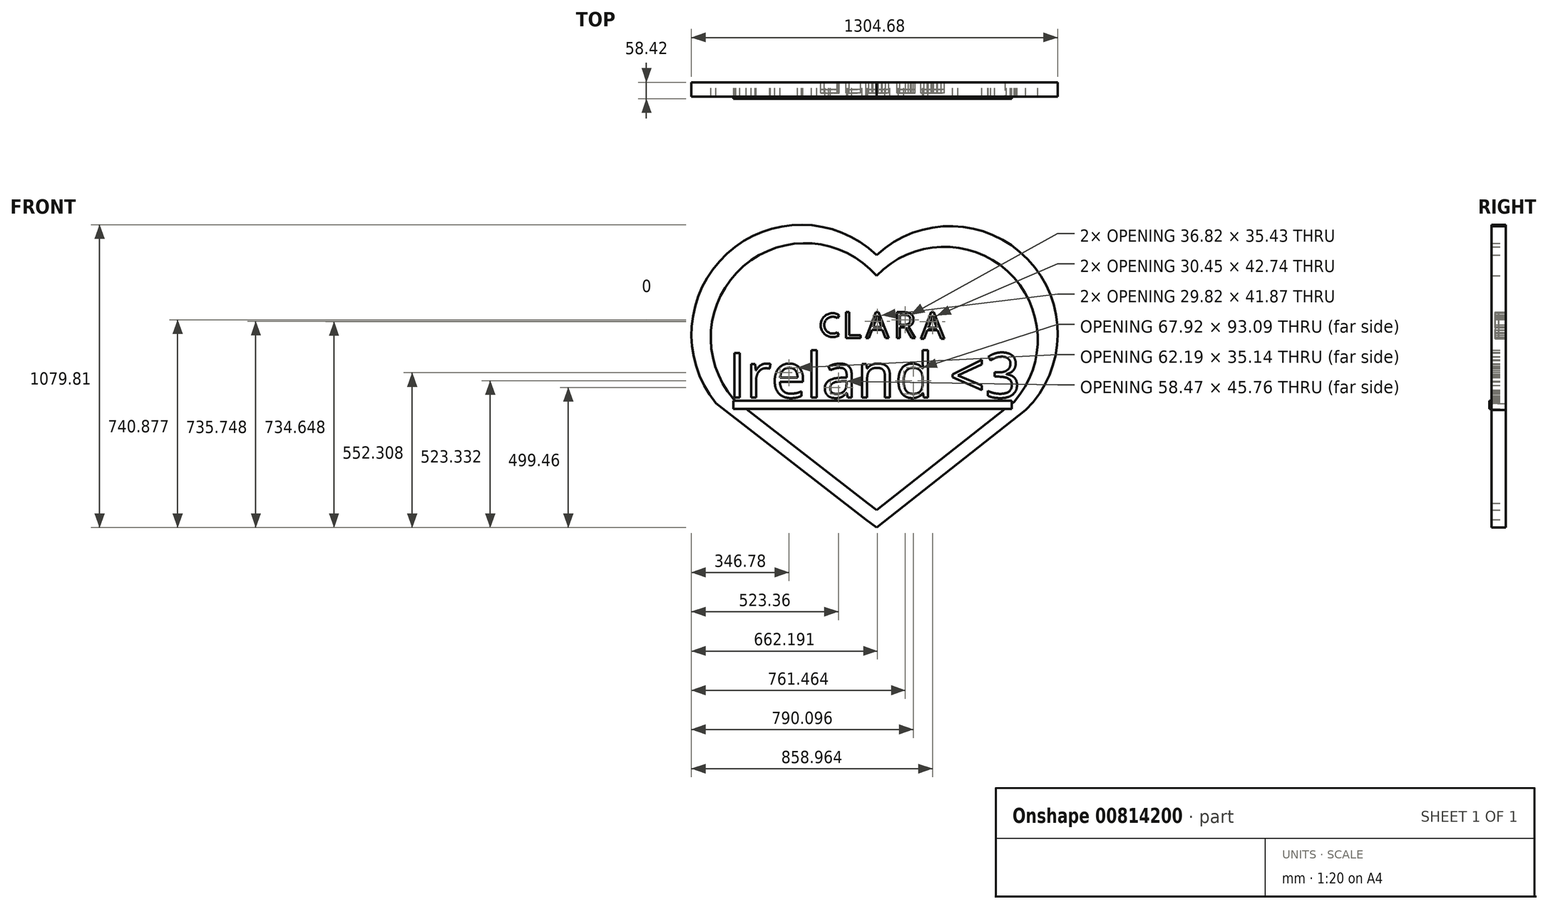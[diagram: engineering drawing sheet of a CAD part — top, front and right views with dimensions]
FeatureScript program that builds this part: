
annotation { "Feature Type Name" : "Feature", "Feature Type Description" : "" }
export const myFeature = defineFeature(function(context is Context, id is Id, definition is map)
    precondition{}
    {
        {
            var Q0;
            Q0=qCreatedBy(makeId("Front.planeOp"),FACE);
            var sketch = newSketch(context, id + "F0", { "sketchPlane" : qUnion([Q0])});
            skArc(sketch, "E0", {"start": v(-133.41, 53.67) * mm, "mid": v(-199.68, 18.4) * mm, "end": v(-134.37, -18.62) * mm});
            skArc(sketch, "E1", {"start": v(-140.44, 43.1) * mm, "mid": v(-186.97, 18.55) * mm, "end": v(-141.67, -8.19) * mm});
            skLineSegment(sketch, "E2", {"start": v(-140.44, 43.1) * mm, "end": v(-133.41, 53.67) * mm});
            skLineSegment(sketch, "E3", {"start": v(-141.67, -8.19) * mm, "end": v(-134.37, -18.62) * mm});
            skText(sketch, "E4", { "text": "R\n", "fontName": "OpenSans-Regular.ttf"});
            skText(sketch, "E5", { "text": "A", "fontName": "OpenSans-Regular.ttf"});
            skText(sketch, "E6", { "text": "A", "fontName": "OpenSans-Regular.ttf"});
            skText(sketch, "E7", { "text": "L", "fontName": "OpenSans-Regular.ttf"});
            const initialGuessF0  = {"E4": [0.05946, -0.02868, 1, 0, 0.09344], "E5": [0.15712, -0.03057, 1, 0, 0.09492], "E6": [-0.0388, -0.02822, 1, 0, 0.09298], "E7": [-0.12193, -0.02824, 1, 0, 0.093]};
            skSetInitialGuess(sketch, initialGuessF0);
            skSolve(sketch);
        }
        {
            var Q0;
            Q0 = qSketchRegion(id + "F0", true);
            extrude(context, id + "F1", {"entities" : qUnion([Q0]), "depth" : 25.4 * mm, "offsetDistance" : 25.4 * mm});
        }
        {
            var Q0;
            Q0=makeQuery(id+"F1.opExtrude","CAP_FACE",FACE,{"disambiguationData":[OSD([sQuery(id+"F0.wireOp",EDGE,"E0"),sQuery(id+"F0.wireOp",EDGE,"E1"),sQuery(id+"F0.wireOp",EDGE,"E2"),sQuery(id+"F0.wireOp",EDGE,"E3")])],"isStart":false});
            var Q1;
            Q1=makeQuery(id+"F1.opExtrude","CAP_FACE",FACE,{"disambiguationData":[OSD([sQuery(id+"F0.wireOp",EDGE,"E7.sketch_text.stroke-0"),sQuery(id+"F0.wireOp",EDGE,"E7.sketch_text.stroke-1"),sQuery(id+"F0.wireOp",EDGE,"E7.sketch_text.stroke-2"),sQuery(id+"F0.wireOp",EDGE,"E7.sketch_text.stroke-3"),sQuery(id+"F0.wireOp",EDGE,"E7.sketch_text.stroke-4"),sQuery(id+"F0.wireOp",EDGE,"E7.sketch_text.stroke-5")])],"isStart":false});
            var Q2;
            Q2=makeQuery(id+"F1.opExtrude","CAP_FACE",FACE,{"disambiguationData":[OSD([sQuery(id+"F0.wireOp",EDGE,"E6.sketch_text.stroke-0"),sQuery(id+"F0.wireOp",EDGE,"E6.sketch_text.stroke-1"),sQuery(id+"F0.wireOp",EDGE,"E6.sketch_text.stroke-2"),sQuery(id+"F0.wireOp",EDGE,"E6.sketch_text.stroke-3"),sQuery(id+"F0.wireOp",EDGE,"E6.sketch_text.stroke-4"),sQuery(id+"F0.wireOp",EDGE,"E6.sketch_text.stroke-5"),sQuery(id+"F0.wireOp",EDGE,"E6.sketch_text.stroke-6"),sQuery(id+"F0.wireOp",EDGE,"E6.sketch_text.stroke-7"),sQuery(id+"F0.wireOp",EDGE,"E6.sketch_text.stroke-8"),sQuery(id+"F0.wireOp",EDGE,"E6.sketch_text.stroke-9"),sQuery(id+"F0.wireOp",EDGE,"E6.sketch_text.stroke-10"),sQuery(id+"F0.wireOp",EDGE,"E6.sketch_text.stroke-11"),sQuery(id+"F0.wireOp",EDGE,"E6.sketch_text.stroke-12")])],"isStart":false});
            var Q3;
            Q3=makeQuery(id+"F1.opExtrude","CAP_FACE",FACE,{"disambiguationData":[OSD([sQuery(id+"F0.wireOp",EDGE,"E4.sketch_text.stroke-0"),sQuery(id+"F0.wireOp",EDGE,"E4.sketch_text.stroke-1"),sQuery(id+"F0.wireOp",EDGE,"E4.sketch_text.stroke-2"),sQuery(id+"F0.wireOp",EDGE,"E4.sketch_text.stroke-3"),sQuery(id+"F0.wireOp",EDGE,"E4.sketch_text.stroke-4"),sQuery(id+"F0.wireOp",EDGE,"E4.sketch_text.stroke-5"),sQuery(id+"F0.wireOp",EDGE,"E4.sketch_text.stroke-6"),sQuery(id+"F0.wireOp",EDGE,"E4.sketch_text.stroke-7"),sQuery(id+"F0.wireOp",EDGE,"E4.sketch_text.stroke-8"),sQuery(id+"F0.wireOp",EDGE,"E4.sketch_text.stroke-9"),sQuery(id+"F0.wireOp",EDGE,"E4.sketch_text.stroke-10"),sQuery(id+"F0.wireOp",EDGE,"E4.sketch_text.stroke-11"),sQuery(id+"F0.wireOp",EDGE,"E4.sketch_text.stroke-12"),sQuery(id+"F0.wireOp",EDGE,"E4.sketch_text.stroke-13"),sQuery(id+"F0.wireOp",EDGE,"E4.sketch_text.stroke-14"),sQuery(id+"F0.wireOp",EDGE,"E4.sketch_text.stroke-15"),sQuery(id+"F0.wireOp",EDGE,"E4.sketch_text.stroke-16"),sQuery(id+"F0.wireOp",EDGE,"E4.sketch_text.stroke-17")])],"isStart":false});
            var Q4;
            Q4=makeQuery(id+"F1.opExtrude","CAP_FACE",FACE,{"disambiguationData":[OSD([sQuery(id+"F0.wireOp",EDGE,"E5.sketch_text.stroke-0"),sQuery(id+"F0.wireOp",EDGE,"E5.sketch_text.stroke-1"),sQuery(id+"F0.wireOp",EDGE,"E5.sketch_text.stroke-2"),sQuery(id+"F0.wireOp",EDGE,"E5.sketch_text.stroke-3"),sQuery(id+"F0.wireOp",EDGE,"E5.sketch_text.stroke-4"),sQuery(id+"F0.wireOp",EDGE,"E5.sketch_text.stroke-5"),sQuery(id+"F0.wireOp",EDGE,"E5.sketch_text.stroke-6"),sQuery(id+"F0.wireOp",EDGE,"E5.sketch_text.stroke-7"),sQuery(id+"F0.wireOp",EDGE,"E5.sketch_text.stroke-8"),sQuery(id+"F0.wireOp",EDGE,"E5.sketch_text.stroke-9"),sQuery(id+"F0.wireOp",EDGE,"E5.sketch_text.stroke-10"),sQuery(id+"F0.wireOp",EDGE,"E5.sketch_text.stroke-11"),sQuery(id+"F0.wireOp",EDGE,"E5.sketch_text.stroke-12")])],"isStart":false});
            extrude(context, id + "F2", {"entities" : qUnion([Q0, Q1, Q2, Q3, Q4]), "depth" : 12.7 * mm, "offsetDistance" : 25.4 * mm});
        }
        {
            var Q0;
            Q0=qCreatedBy(makeId("Front.planeOp"),FACE);
            var sketch = newSketch(context, id + "F3", { "sketchPlane" : qUnion([Q0])});
            skText(sketch, "E8", { "text": "Ireland <3", "fontName": "OpenSans-Regular.ttf"});
            const initialGuessF3  = {"E8": [-0.52864, -0.2402, 1, 0, 0.16]};
            skSetInitialGuess(sketch, initialGuessF3);
            skSolve(sketch);
        }
        {
            var Q0;
            Q0=makeQuery(id+"F3.imprint","IMPRINT",FACE,{"disambiguationData":[TD([[makeQuery(id+"F3.imprint","IMPRINT",EDGE,{"derivedFrom":sQuery(id+"F3.wireOp",EDGE,"E8.sketch_text.stroke-0")}),-1.0]])]});
            var Q1;
            Q1=makeQuery(id+"F3.imprint","IMPRINT",FACE,{"disambiguationData":[TD([[makeQuery(id+"F3.imprint","IMPRINT",EDGE,{"derivedFrom":sQuery(id+"F3.wireOp",EDGE,"E8.sketch_text.stroke-36")}),-1.0]])]});
            var Q2;
            Q2=makeQuery(id+"F3.imprint","IMPRINT",FACE,{"disambiguationData":[TD([[makeQuery(id+"F3.imprint","IMPRINT",EDGE,{"derivedFrom":sQuery(id+"F3.wireOp",EDGE,"E8.sketch_text.stroke-67")}),-1.0]])]});
            var Q3;
            Q3=makeQuery(id+"F3.imprint","IMPRINT",FACE,{"disambiguationData":[TD([[makeQuery(id+"F3.imprint","IMPRINT",EDGE,{"derivedFrom":sQuery(id+"F3.wireOp",EDGE,"E8.sketch_text.stroke-108")}),-1.0]])]});
            var Q4;
            Q4=makeQuery(id+"F3.imprint","IMPRINT",FACE,{"disambiguationData":[TD([[makeQuery(id+"F3.imprint","IMPRINT",EDGE,{"derivedFrom":sQuery(id+"F3.wireOp",EDGE,"E8.sketch_text.stroke-115")}),-1.0]])]});
            var Q5;
            Q5=makeQuery(id+"F3.imprint","IMPRINT",FACE,{"disambiguationData":[TD([[makeQuery(id+"F3.imprint","IMPRINT",EDGE,{"derivedFrom":sQuery(id+"F3.wireOp",EDGE,"E8.sketch_text.stroke-17")}),-1.0]])]});
            var Q6;
            Q6=makeQuery(id+"F3.imprint","IMPRINT",FACE,{"disambiguationData":[TD([[makeQuery(id+"F3.imprint","IMPRINT",EDGE,{"derivedFrom":sQuery(id+"F3.wireOp",EDGE,"E8.sketch_text.stroke-40")}),-1.0]])]});
            var Q7;
            Q7=makeQuery(id+"F3.imprint","IMPRINT",FACE,{"disambiguationData":[TD([[makeQuery(id+"F3.imprint","IMPRINT",EDGE,{"derivedFrom":sQuery(id+"F3.wireOp",EDGE,"E8.sketch_text.stroke-84")}),-1.0]])]});
            var Q8;
            Q8=makeQuery(id+"F3.imprint","IMPRINT",FACE,{"disambiguationData":[TD([[makeQuery(id+"F3.imprint","IMPRINT",EDGE,{"derivedFrom":sQuery(id+"F3.wireOp",EDGE,"E8.sketch_text.stroke-4")}),-1.0]])]});
            extrude(context, id + "F4", {"entities" : qUnion([Q0, Q1, Q2, Q3, Q4, Q5, Q6, Q7, Q8]), "depth" : 50.8 * mm, "offsetDistance" : 25.4 * mm});
        }
        {
            var Q0;
            Q0=qCreatedBy(makeId("Front.planeOp"),FACE);
            var sketch = newSketch(context, id + "F5", { "sketchPlane" : qUnion([Q0])});
            skLineSegment(sketch, "E9.bottom", {"start": v(-510.24, -251.9) * mm, "end": v(480.57, -251.9) * mm});
            skLineSegment(sketch, "E9.top", {"start": v(-510.24, -281.46) * mm, "end": v(480.57, -281.46) * mm});
            skLineSegment(sketch, "E9.left", {"start": v(-510.24, -251.9) * mm, "end": v(-510.24, -281.46) * mm});
            skLineSegment(sketch, "E9.right", {"start": v(480.57, -251.9) * mm, "end": v(480.57, -281.46) * mm});
            skLineSegment(sketch, "E10", {"start": v(-510.24, -266.68) * mm, "end": v(480.57, -266.68) * mm});
            skSolve(sketch);
        }
        {
            var Q0;
            {var subQ0=sQuery(id+"F5.wireOp",EDGE,"E9.bottom");Q0=makeQuery(id+"F5.imprint","IMPRINT",FACE,{"disambiguationData":[TD([[makeQuery(id+"F5.imprint","IMPRINT",EDGE,{"derivedFrom":subQ0}),-1.0]])]});}
            var Q1;
            {var subQ0=sQuery(id+"F5.wireOp",EDGE,"E9.top");Q1=makeQuery(id+"F5.imprint","IMPRINT",FACE,{"disambiguationData":[TD([[makeQuery(id+"F5.imprint","IMPRINT",EDGE,{"derivedFrom":subQ0}),1.0]])]});}
            extrude(context, id + "F6", {"entities" : qUnion([Q0, Q1]), "depth" : 58.42 * mm, "offsetDistance" : 25.4 * mm});
        }
        {
            var Q0;
            Q0=qCreatedBy(makeId("Front.planeOp"),FACE);
            var sketch = newSketch(context, id + "F7", { "sketchPlane" : qUnion([Q0])});
            skArc(sketch, "E11", {"start": v(0, 193.44) * mm, "mid": v(-474.7, 228.23) * mm, "end": v(-509.5, -246.47) * mm});
            skArc(sketch, "E12", {"start": v(489.32, -255.63) * mm, "mid": v(466.04, 210.13) * mm, "end": v(0, 193.44) * mm});
            skLineSegment(sketch, "E13", {"start": v(-509.5, -246.47) * mm, "end": v(-32, -617.75) * mm});
            skLineSegment(sketch, "E14", {"start": v(-32, -617.75) * mm, "end": v(0, -642) * mm});
            skLineSegment(sketch, "E15", {"start": v(0, -642) * mm, "end": v(489.32, -255.63) * mm});
            skSolve(sketch);
        }
        {
            var Q0;
            Q0=makeQuery(id+"F7.imprint","IMPRINT",FACE,{"disambiguationData":[TD([[makeQuery(id+"F7.imprint","IMPRINT",EDGE,{"derivedFrom":sQuery(id+"F7.wireOp",EDGE,"E11")}),1.0]])]});
            var sketch = newSketch(context, id + "F8", { "sketchPlane" : qUnion([Q0])});
            skLineSegment(sketch, "E16", {"start": v(-38.83, -675.89) * mm, "end": v(-573.54, -260.12) * mm});
            skArc(sketch, "E17", {"start": v(0, 267.94) * mm, "mid": v(-534.05, 272.48) * mm, "end": v(-573.54, -260.12) * mm});
            skLineSegment(sketch, "E18", {"start": v(0, -704.07) * mm, "end": v(-38.83, -675.89) * mm});
            skLineSegment(sketch, "E19", {"start": v(0, -704.07) * mm, "end": v(530.68, -285.03) * mm});
            skArc(sketch, "E20", {"start": v(530.68, -285.03) * mm, "mid": v(537.85, 252.99) * mm, "end": v(0, 267.94) * mm});
            skSolve(sketch);
        }
        {
            var Q0;
            Q0=makeQuery(id+"F8.imprint","IMPRINT",FACE,{"disambiguationData":[TD([[makeQuery(id+"F8.imprint","IMPRINT",EDGE,{"derivedFrom":sQuery(id+"F8.wireOp",EDGE,"E16")}),-1.0]])]});
            extrude(context, id + "F9", {"entities" : qUnion([Q0]), "operationType" : NewBodyOperationType.ADD, "depth" : 50.8 * mm, "offsetDistance" : 25.4 * mm});
        }
    });
